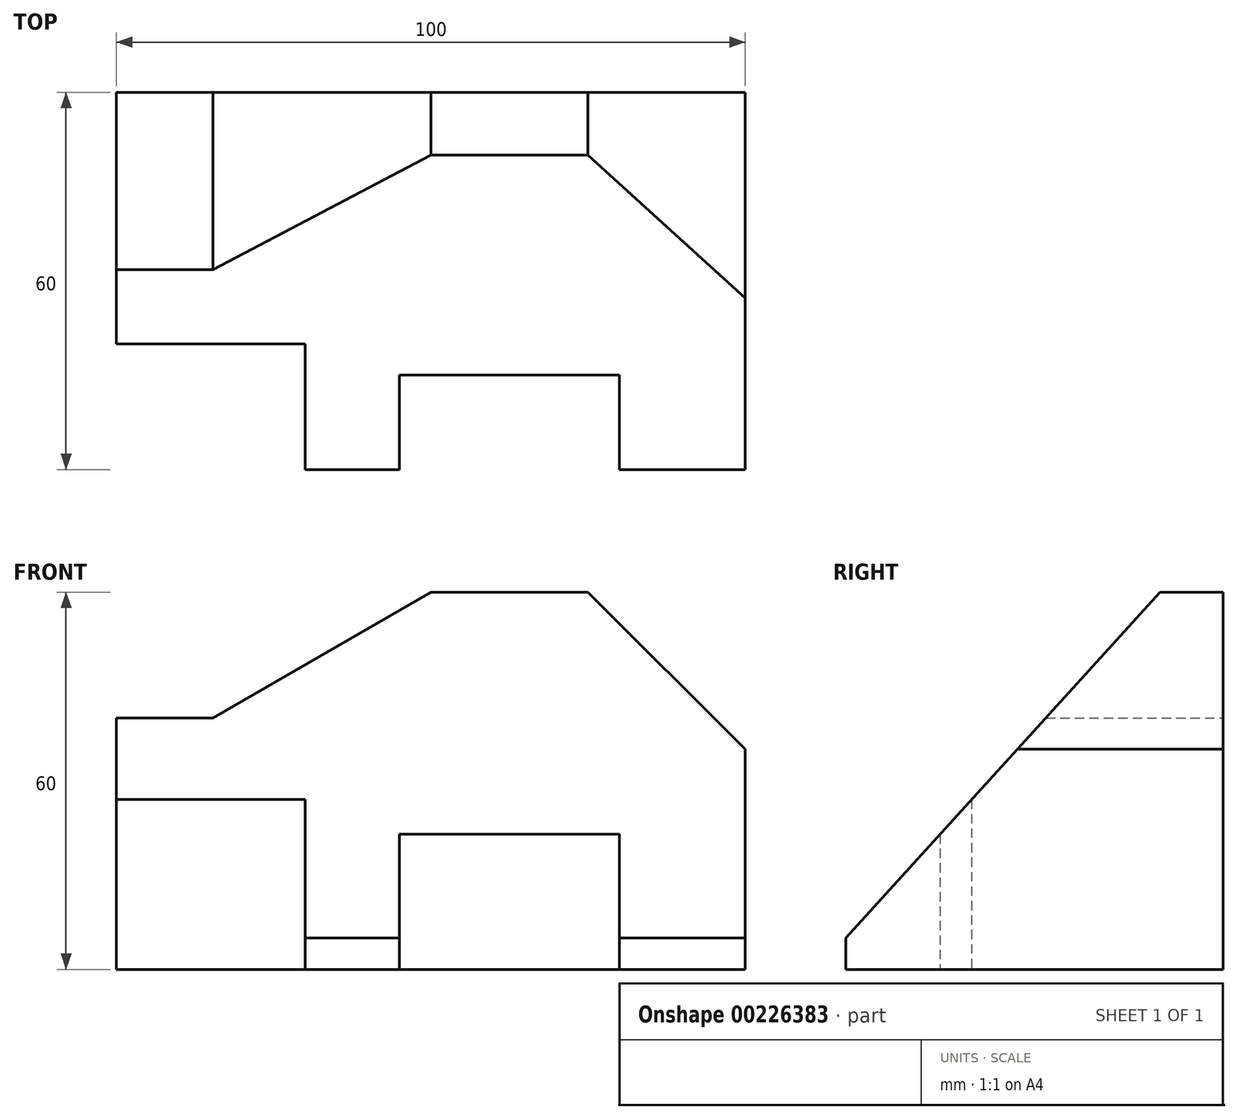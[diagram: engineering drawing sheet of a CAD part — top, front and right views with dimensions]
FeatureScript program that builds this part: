
annotation { "Feature Type Name" : "Feature", "Feature Type Description" : "" }
export const myFeature = defineFeature(function(context is Context, id is Id, definition is map)
    precondition{}
    {
        {
            var Q0;
            Q0=qCreatedBy(makeId("Right.planeOp"),FACE);
            var sketch = newSketch(context, id + "F0", { "sketchPlane" : qUnion([Q0])});
            skLineSegment(sketch, "E0", {"start": v(0, 0) * mm, "end": v(60, 0) * mm});
            skLineSegment(sketch, "E1", {"start": v(60, 0) * mm, "end": v(60, 60) * mm});
            skLineSegment(sketch, "E2", {"start": v(60, 60) * mm, "end": v(50, 60) * mm});
            skLineSegment(sketch, "E3", {"start": v(50, 60) * mm, "end": v(0, 5) * mm});
            skLineSegment(sketch, "E4", {"start": v(0, 5) * mm, "end": v(0, 0) * mm});
            skSolve(sketch);
        }
        {
            var Q0;
            Q0=makeQuery(id+"F0.imprint","IMPRINT",FACE,{"disambiguationData":[TD([[makeQuery(id+"F0.imprint","IMPRINT",EDGE,{"derivedFrom":sQuery(id+"F0.wireOp",EDGE,"E0")}),1.0]])]});
            extrude(context, id + "F1", {"entities" : qUnion([Q0]), "endBound" : BoundingType.SYMMETRIC, "depth" : 100 * mm});
        }
        {
            var Q0;
            Q0=makeQuery(id+"F1.opExtrude","SWEPT_FACE",FACE,{"disambiguationData":[OSD([sQuery(id+"F0.wireOp",EDGE,"E0")])]});
            var sketch = newSketch(context, id + "F2", { "sketchPlane" : qUnion([Q0])});
            skLineSegment(sketch, "E5.bottom", {"start": v(-50, 0) * mm, "end": v(-20, 0) * mm});
            skLineSegment(sketch, "E5.top", {"start": v(-50, -20) * mm, "end": v(-20, -20) * mm});
            skLineSegment(sketch, "E5.left", {"start": v(-50, 0) * mm, "end": v(-50, -20) * mm});
            skLineSegment(sketch, "E5.right", {"start": v(-20, 0) * mm, "end": v(-20, -20) * mm});
            skLineSegment(sketch, "E6.bottom", {"start": v(30, 0) * mm, "end": v(-5, 0) * mm});
            skLineSegment(sketch, "E6.top", {"start": v(30, -15) * mm, "end": v(-5, -15) * mm});
            skLineSegment(sketch, "E6.left", {"start": v(30, 0) * mm, "end": v(30, -15) * mm});
            skLineSegment(sketch, "E6.right", {"start": v(-5, 0) * mm, "end": v(-5, -15) * mm});
            skSolve(sketch);
        }
        {
            var Q0;
            Q0=makeQuery(id+"F2.imprint","IMPRINT",FACE,{"disambiguationData":[TD([[makeQuery(id+"F2.imprint","IMPRINT",EDGE,{"derivedFrom":sQuery(id+"F2.wireOp",EDGE,"E6.bottom")}),1.0]])]});
            var Q1;
            Q1=makeQuery(id+"F2.imprint","IMPRINT",FACE,{"disambiguationData":[TD([[makeQuery(id+"F2.imprint","IMPRINT",EDGE,{"derivedFrom":sQuery(id+"F2.wireOp",EDGE,"E5.bottom")}),1.0]])]});
            extrude(context, id + "F3", {"entities" : qUnion([Q0, Q1]), "operationType" : NewBodyOperationType.REMOVE, "endBound" : BoundingType.THROUGH_ALL, "oppositeDirection" : true, "depth" : 25 * mm});
        }
        {
            var Q0;
            Q0=makeQuery(id+"F1.opExtrude","SWEPT_FACE",FACE,{"disambiguationData":[OSD([sQuery(id+"F0.wireOp",EDGE,"E1")])]});
            var sketch = newSketch(context, id + "F4", { "sketchPlane" : qUnion([Q0])});
            skLineSegment(sketch, "E7", {"start": v(-50, 60) * mm, "end": v(-50, 35) * mm});
            skLineSegment(sketch, "E8", {"start": v(-50, 35) * mm, "end": v(-25, 60) * mm});
            skLineSegment(sketch, "E9", {"start": v(-25, 60) * mm, "end": v(-50, 60) * mm});
            skLineSegment(sketch, "E10", {"start": v(0, 60) * mm, "end": v(50, 60) * mm});
            skLineSegment(sketch, "E11", {"start": v(50, 60) * mm, "end": v(50, 40) * mm});
            skLineSegment(sketch, "E12", {"start": v(50, 40) * mm, "end": v(34.64, 40) * mm});
            skLineSegment(sketch, "E13", {"start": v(34.64, 40) * mm, "end": v(0, 60) * mm});
            skSolve(sketch);
        }
        {
            var Q0;
            Q0=makeQuery(id+"F4.imprint","IMPRINT",FACE,{"disambiguationData":[TD([[makeQuery(id+"F4.imprint","IMPRINT",EDGE,{"derivedFrom":sQuery(id+"F4.wireOp",EDGE,"E10")}),-1.0]])]});
            var Q1;
            Q1=makeQuery(id+"F4.imprint","IMPRINT",FACE,{"disambiguationData":[TD([[makeQuery(id+"F4.imprint","IMPRINT",EDGE,{"derivedFrom":sQuery(id+"F4.wireOp",EDGE,"E7")}),-1.0]])]});
            extrude(context, id + "F5", {"entities" : qUnion([Q0, Q1]), "operationType" : NewBodyOperationType.REMOVE, "endBound" : BoundingType.THROUGH_ALL, "oppositeDirection" : true, "depth" : 25 * mm});
        }
    });
